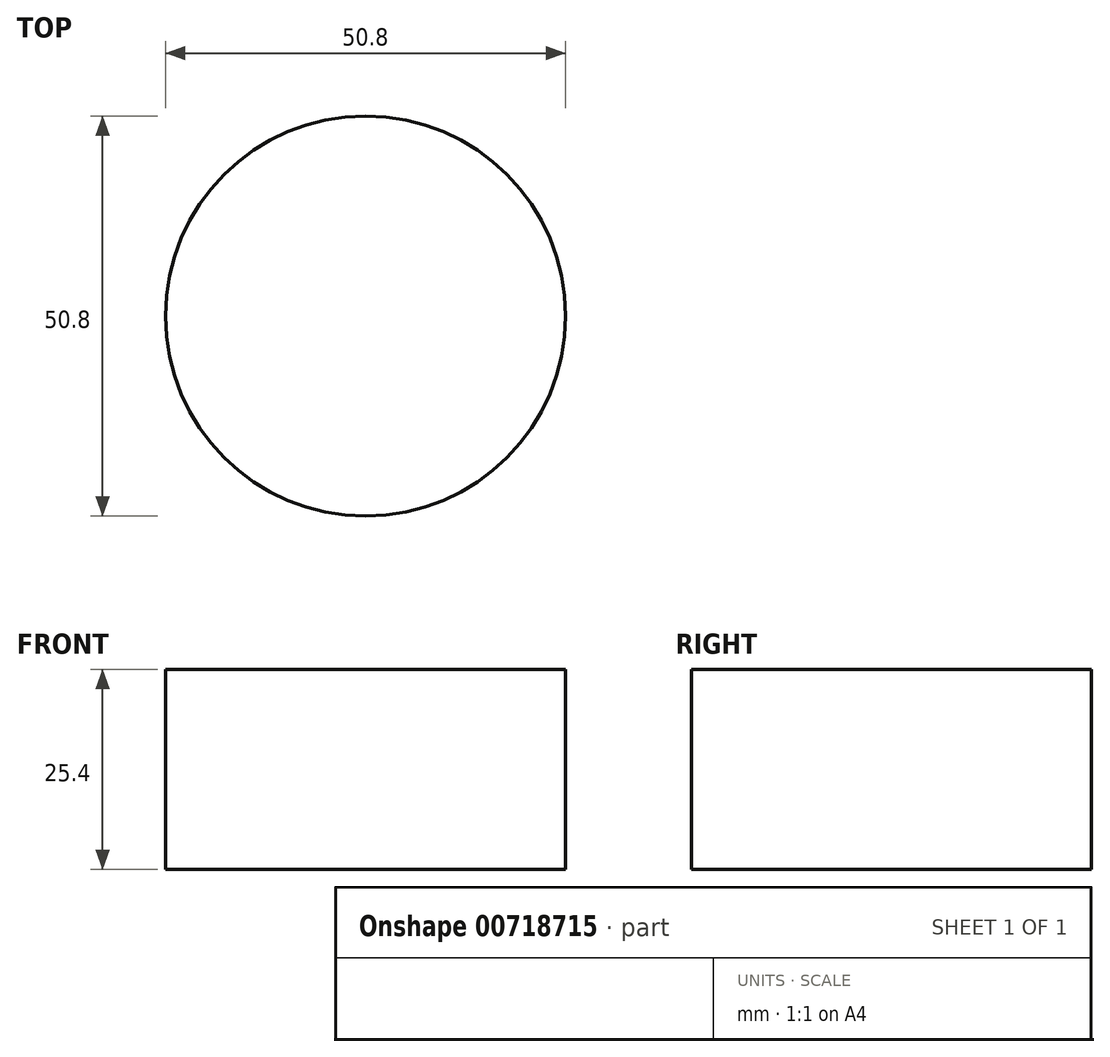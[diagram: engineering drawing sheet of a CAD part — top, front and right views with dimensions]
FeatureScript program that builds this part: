
annotation { "Feature Type Name" : "Feature", "Feature Type Description" : "" }
export const myFeature = defineFeature(function(context is Context, id is Id, definition is map)
    precondition{}
    {
        {
            var Q0;
            Q0=qCreatedBy(makeId("Top.planeOp"),FACE);
            var sketch = newSketch(context, id + "F0", { "sketchPlane" : qUnion([Q0])});
            skCircle(sketch, "E0", {"center": v(0, 0) * mm, "radius": 25.4 * mm});
            skSolve(sketch);
        }
        {
            var Q0;
            Q0 = qSketchRegion(id + "F0", true);
            extrude(context, id + "F1", {"entities" : qUnion([Q0]), "depth" : 25.4 * mm, "offsetDistance" : 25.4 * mm});
        }
    });
